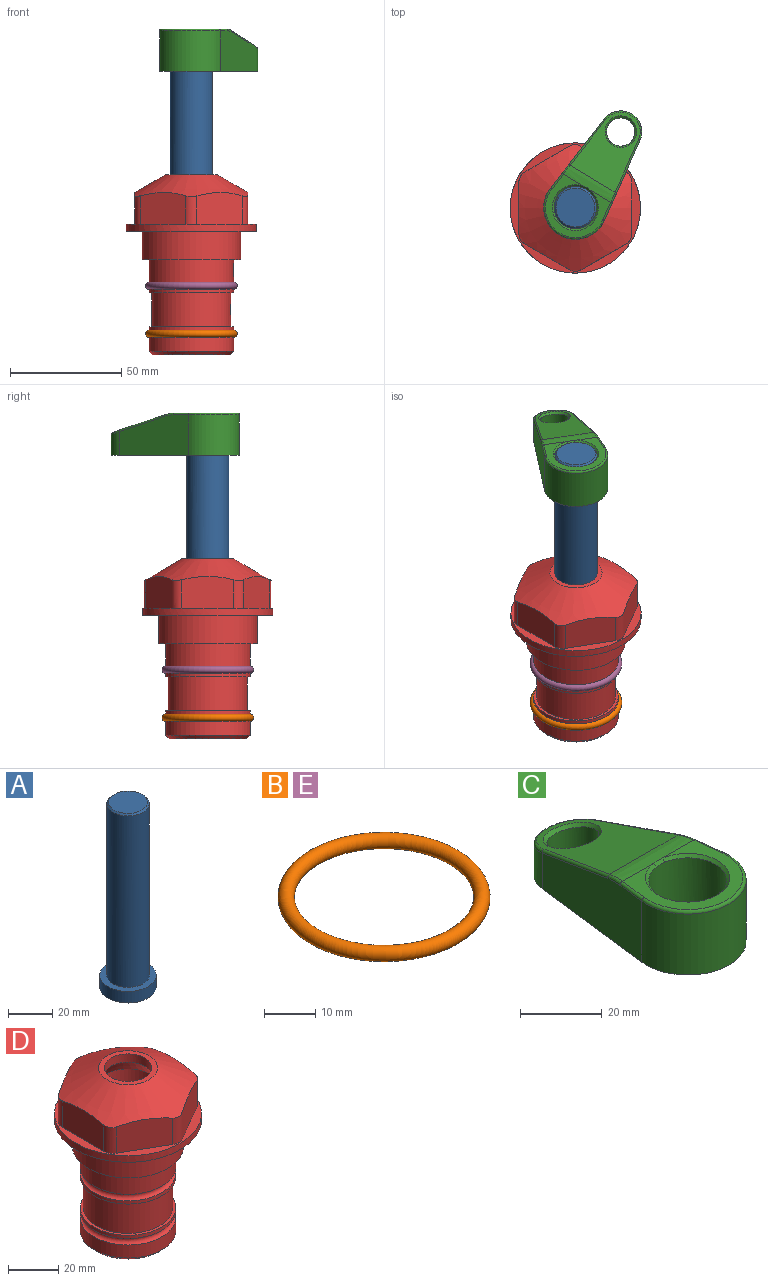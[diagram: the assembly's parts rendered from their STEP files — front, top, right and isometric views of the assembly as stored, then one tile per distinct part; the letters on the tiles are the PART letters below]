
ASSEMBLY  parts=5 mates=4
PART A: 6 faces, bbox 25.4x25.4x101.6 mm
  f0: plane 17.46x17.46mm, normal (0,0,1), area 239.5mm2, adj f5
  f1: plane 25.4x25.4mm, normal (0,0,-1), area 506.7mm2, adj f2
  f2: cylinder r=12.7mm len=25.4mm, axis (0,0,1), area 506.7mm2, adj f1,f3
  f3: plane 25.4x25.4mm, normal (0,0,1), area 221.7mm2, adj f2,f4
  f4: cylinder r=9.53mm len=94.46mm, axis (0,0,1), area 5653mm2, adj f3,f5
  f5: cone r=8.73mm half-angle=45deg, axis (0,0,-1), area 64.4mm2, adj f0,f4
PART B: 1 faces, bbox 44.7x44.7x3.2 mm
  f0: torus R=19.05mm, axis (0,0,1), area 1193.9mm2
PART C: 31 faces, bbox 31.7x65.5x19.8 mm
  f0: plane 39.12x18.26mm, normal (0.99,0.12,0), area 612.2mm2, adj f1,f4,f7,f11,f13,f15
  f1: cylinder r=9.53mm len=18.91mm, axis (0,0,-1), area 296.1mm2, adj f0,f2,f7,f17
  f2: plane 39.12x18.26mm, normal (-0.99,0.12,0), area 612.2mm2, adj f1,f4,f7,f12,f14,f16
  f3: cylinder r=6.35mm len=12.7mm, axis (0,0,-1), area 362.4mm2, adj f7,f18
  f4: cylinder r=14.29mm len=28.58mm, axis (0,0,-1), area 882.2mm2, adj f0,f2,f7,f10
  f5: cylinder r=9.53mm len=19.05mm, axis (0,0,-1), area 1092.6mm2, adj f7,f19,f20
  f6: plane 26.99x23.69mm, normal (0,0,1), area 216.2mm2, adj f9,f10,f11,f12,f19
  f7: plane 63.5x28.58mm, normal (0,0,-1), area 661.8mm2, adj f0,f1,f2,f3,f4,f5,f22,f23
  f8: plane 33.52x23.6mm, normal (0,0.26,0.97), area 486mm2, adj f9,f15,f16,f17,f18
  f9: cylinder r=19.05mm len=24.72mm, axis (1,0,0), area 120.4mm2, adj f6,f8,f13,f14,f20
  f10: torus R=13.49mm, axis (0,0,1), area 59mm2, adj f4,f6,f11,f12
  f11: cylinder r=0.79mm len=8.67mm, axis (0.12,-0.99,0), area 10.8mm2, adj f0,f6,f10,f13
  f12: cylinder r=0.79mm len=8.67mm, axis (0.12,0.99,0), area 10.8mm2, adj f2,f6,f10,f14
  f13: bspline ~4.95x1.42mm, area 6.1mm2, adj f0,f9,f11,f15
  f14: bspline ~4.95x1.42mm, area 6.1mm2, adj f2,f9,f12,f16
  f15: cylinder r=0.79mm len=25.95mm, axis (0.12,-0.96,0.26), area 32.9mm2, adj f0,f8,f13,f17
  f16: cylinder r=0.79mm len=25.95mm, axis (0.12,0.96,-0.26), area 32.9mm2, adj f2,f8,f14,f17
  f17: bspline ~18.91x8.38mm, area 30mm2, adj f1,f8,f15,f16
  f18: bspline ~14.29x14.29mm, area 48.3mm2, adj f3,f8
  f19: cone r=9.53mm half-angle=45deg, axis (0,0,1), area 66.5mm2, adj f5,f6,f20
  f20: bspline ~3.22x0.96mm, area 3.5mm2, adj f5,f9,f19
  f21: plane 2.75x2.72mm, normal (0,0,-1), area 2.9mm2, adj f23,f25,f28
  f22: plane 23.05x15.88mm, normal (-0.99,-0.12,0), area 323.6mm2, adj f7,f25,f26,f27,f28,f29
  f23: plane 23.05x15.88mm, normal (0.99,-0.12,0), area 323.6mm2, adj f7,f21,f25,f27,f28,f30
  f24: cylinder r=9.53mm len=10.69mm, axis (0,0,-1), area 114.7mm2, adj f7,f27,f29,f30
  f25: cylinder r=12.7mm len=20.59mm, axis (0,0,-1), area 381.1mm2, adj f7,f21,f22,f23,f26,f28
  f26: plane 2.75x2.72mm, normal (0,0,-1), area 2.9mm2, adj f22,f25,f28
  f27: plane 19.72x18.37mm, normal (0,-0.26,-0.97), area 291.8mm2, adj f22,f23,f24,f28,f29,f30
  f28: cylinder r=15.88mm len=19.92mm, axis (1,0,0), area 54.8mm2, adj f21,f22,f23,f25,f26,f27
  f29: cylinder r=1.59mm len=11mm, axis (0,0,-1), area 34.7mm2, adj f7,f22,f24,f27
  f30: cylinder r=1.59mm len=11mm, axis (0,0,-1), area 34.7mm2, adj f7,f23,f24,f27
PART D: 36 faces, bbox 58.7x58.7x81 mm
  f0: cylinder r=17.78mm len=35.56mm, axis (0,0,1), area 1670.8mm2, adj f23,f24,f31
  f1: cylinder r=19.05mm len=38.1mm, axis (0,0,1), area 1191.9mm2, adj f26,f27,f30
  f2: plane 58.66x58.66mm, normal (0,0,-1), area 1150.6mm2, adj f3,f28
  f3: cylinder r=29.33mm len=58.66mm, axis (0,0,-1), area 585.1mm2, adj f2,f4
  f4: plane 58.66x58.66mm, normal (0,0,1), area 475.9mm2, adj f3,f5,f6,f7,f8,f9,f10,f11
  f5: plane 20.32x14.34mm, normal (-0.5,0.87,0), area 324.4mm2, adj f4,f15,f16,f17
  f6: plane 20.32x14.34mm, normal (0.5,0.87,0), area 324.4mm2, adj f4,f14,f15,f17
  f7: plane 23.48x14.34mm, normal (1,0,0), area 324.4mm2, adj f4,f13,f14,f17
  f8: plane 20.32x14.34mm, normal (0.5,-0.87,0), area 324.4mm2, adj f4,f12,f13,f17
  f9: plane 20.32x14.34mm, normal (-0.5,-0.87,0), area 324.4mm2, adj f4,f11,f12,f17
  f10: plane 23.48x14.34mm, normal (-1,0,0), area 324.4mm2, adj f4,f11,f16,f17
  f11: cylinder r=5.08mm len=12.85mm, axis (0,0,-1), area 67.2mm2, adj f4,f9,f10,f17
  f12: cylinder r=5.08mm len=12.85mm, axis (0,0,-1), area 67.2mm2, adj f4,f8,f9,f17
  f13: cylinder r=5.08mm len=12.85mm, axis (0,0,-1), area 67.2mm2, adj f4,f7,f8,f17
  f14: cylinder r=5.08mm len=12.85mm, axis (0,0,-1), area 67.2mm2, adj f4,f6,f7,f17
  f15: cylinder r=5.08mm len=12.85mm, axis (0,0,-1), area 67.2mm2, adj f4,f5,f6,f17
  f16: cylinder r=5.08mm len=12.85mm, axis (0,0,-1), area 67.2mm2, adj f4,f5,f10,f17
  f17: cone r=11.73mm half-angle=60deg, axis (0,0,-1), area 2071.8mm2, adj f5,f6,f7,f8,f9,f10,f11,f12
  f18: plane 23.46x23.46mm, normal (0,0,1), area 147.4mm2, adj f17,f35
  f19: plane 34.93x34.93mm, normal (0,0,-1), area 958mm2, adj f29
  f20: cylinder r=19.05mm len=38.1mm, axis (0,0,1), area 760.1mm2, adj f21,f29
  f21: torus R=19.05mm, axis (0,0,1), area 565.3mm2, adj f20,f22
  f22: cylinder r=19.05mm len=38.1mm, axis (0,0,1), area 190mm2, adj f21,f23
  f23: plane 38.1x38.1mm, normal (0,0,1), area 146.9mm2, adj f0,f22
  f24: plane 38.1x38.1mm, normal (0,0,-1), area 146.9mm2, adj f0,f25
  f25: cylinder r=19.05mm len=38.1mm, axis (0,0,1), area 190mm2, adj f24,f26
  f26: torus R=19.05mm, axis (0,0,1), area 565.3mm2, adj f1,f25
  f27: plane 44.45x44.45mm, normal (0,0,-1), area 411.7mm2, adj f1,f28
  f28: cylinder r=22.23mm len=44.45mm, axis (0,0,1), area 1773.5mm2, adj f2,f27
  f29: cone r=19.05mm half-angle=45deg, axis (0,0,1), area 257.5mm2, adj f19,f20
  f30: cylinder r=3.17mm len=6.75mm, axis (-1,0,0), area 128mm2, adj f1,f33
  f31: cylinder r=3.17mm len=6.35mm, axis (-1,0,0), area 102.5mm2, adj f0,f33
  f32: plane 25.4x25.4mm, normal (0,0,1), area 506.7mm2, adj f33
  f33: cylinder r=12.7mm len=66.42mm, axis (0,0,-1), area 5236.2mm2, adj f30,f31,f32,f34
  f34: cone r=9.53mm half-angle=30deg, axis (0,0,-1), area 443.4mm2, adj f33,f35
  f35: cylinder r=9.53mm len=19.05mm, axis (0,0,-1), area 240.9mm2, adj f18,f34
PART E: same geometry as B
PLACE A rot(axis=(0,0,-1),30.9deg) t=(0,0,27.55)mm
PLACE B t=(0,0,-21.59)mm
PLACE C rot(axis=(0,0,-1),30.9deg) t=(0,0,27.55)mm
PLACE D at identity fixed
PLACE E at identity
MATE fastened E.f0 <-> D.f0  axis (0,0,1) through (0,0,-24.51)mm
MATE cylindrical A.f2 <-> D.f0  axis (0,0,-1) through (0,0,-10.55)mm
MATE fastened A.f2 <-> C.f4  axis (0,0,1) through (0,0,91.05)mm
MATE fastened B.f0 <-> D.f0  axis (0,0,1) through (0,0,-46.1)mm
